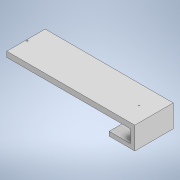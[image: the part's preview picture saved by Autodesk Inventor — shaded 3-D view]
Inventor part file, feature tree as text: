
AUTODESK INVENTOR PART (.ipt)
format: ipt  version: 2022 (Build 260153000, 153)  size: 138,752 bytes
history: native  units: mm
features: extrude x5, sketch x5
ambient origin geometry x8: Origin, YZ Plane, XZ Plane, XY Plane, X Axis, Y Axis, Z Axis, Center Point
bodies: Solid1 (feature_tree)
feature tree (10):
  extrude  "Extrusion1"  Depth=10.0mm
  extrude  "Extrusion4"  Depth=40.0mm
  sketch  "Sketch5"  dims[d4=300.0mm d5=15.0mm]
  extrude  "Extrusion6"  Depth=300.0mm
  extrude  "Extrusion7"  Depth=2.0mm
  extrude  "Extrusion8"  Depth=90.0mm
  sketch  "Sketch1"  dims[d0=50.0mm d1=10.0mm]
  sketch  "Sketch4"  dims[d2=10.0mm d3=40.0mm]
  sketch  "Sketch6"  dims[d6=90.0mm d7=0.0mm d17=2.0mm]
  sketch  "Sketch7"  dims[d18=10.0mm d19=0.0mm d25=90.0mm d26=2.5mm d27=300.0mm d28=0.0mm d29=3.0mm d30=60.0mm d31=0.0mm d32=75.0mm d33=5.0mm d34=55.0mm d35=250.0mm d36=0.0mm]
